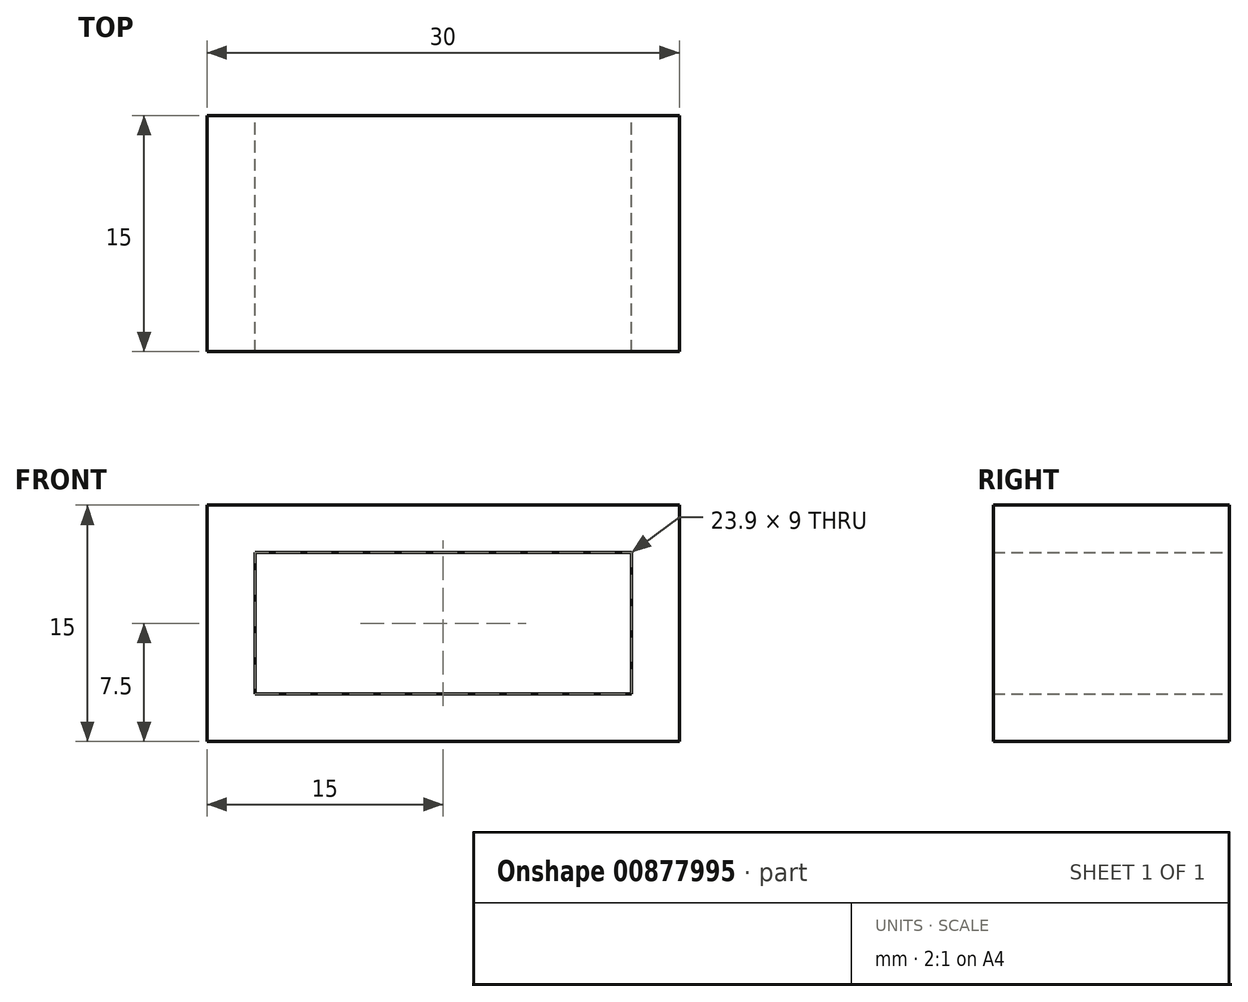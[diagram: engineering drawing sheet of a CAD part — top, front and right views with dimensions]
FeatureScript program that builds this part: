
annotation { "Feature Type Name" : "Feature", "Feature Type Description" : "" }
export const myFeature = defineFeature(function(context is Context, id is Id, definition is map)
    precondition{}
    {
        {
            var Q0;
            Q0=qCreatedBy(makeId("Front.planeOp"),FACE);
            var sketch = newSketch(context, id + "F0", { "sketchPlane" : qUnion([Q0])});
            skLineSegment(sketch, "E0.bottom", {"start": v(-15, 7.5) * mm, "end": v(15, 7.5) * mm});
            skLineSegment(sketch, "E0.top", {"start": v(-15, -7.5) * mm, "end": v(15, -7.5) * mm});
            skLineSegment(sketch, "E0.left", {"start": v(-15, 7.5) * mm, "end": v(-15, -7.5) * mm});
            skLineSegment(sketch, "E0.right", {"start": v(15, 7.5) * mm, "end": v(15, -7.5) * mm});
            skLineSegment(sketch, "E1.bottom", {"start": v(-11.95, 4.5) * mm, "end": v(11.95, 4.5) * mm});
            skLineSegment(sketch, "E1.top", {"start": v(-11.95, -4.5) * mm, "end": v(11.95, -4.5) * mm});
            skLineSegment(sketch, "E1.left", {"start": v(-11.95, 4.5) * mm, "end": v(-11.95, -4.5) * mm});
            skLineSegment(sketch, "E1.right", {"start": v(11.95, 4.5) * mm, "end": v(11.95, -4.5) * mm});
            skSolve(sketch);
        }
        {
            var Q0;
            Q0=makeQuery(id+"F0.imprint","IMPRINT",FACE,{"disambiguationData":[TD([[makeQuery(id+"F0.imprint","IMPRINT",EDGE,{"derivedFrom":sQuery(id+"F0.wireOp",EDGE,"E0.bottom")}),-1.0]])]});
            extrude(context, id + "F1", {"entities" : qUnion([Q0]), "depth" : 15 * mm, "offsetDistance" : 25 * mm});
        }
    });
